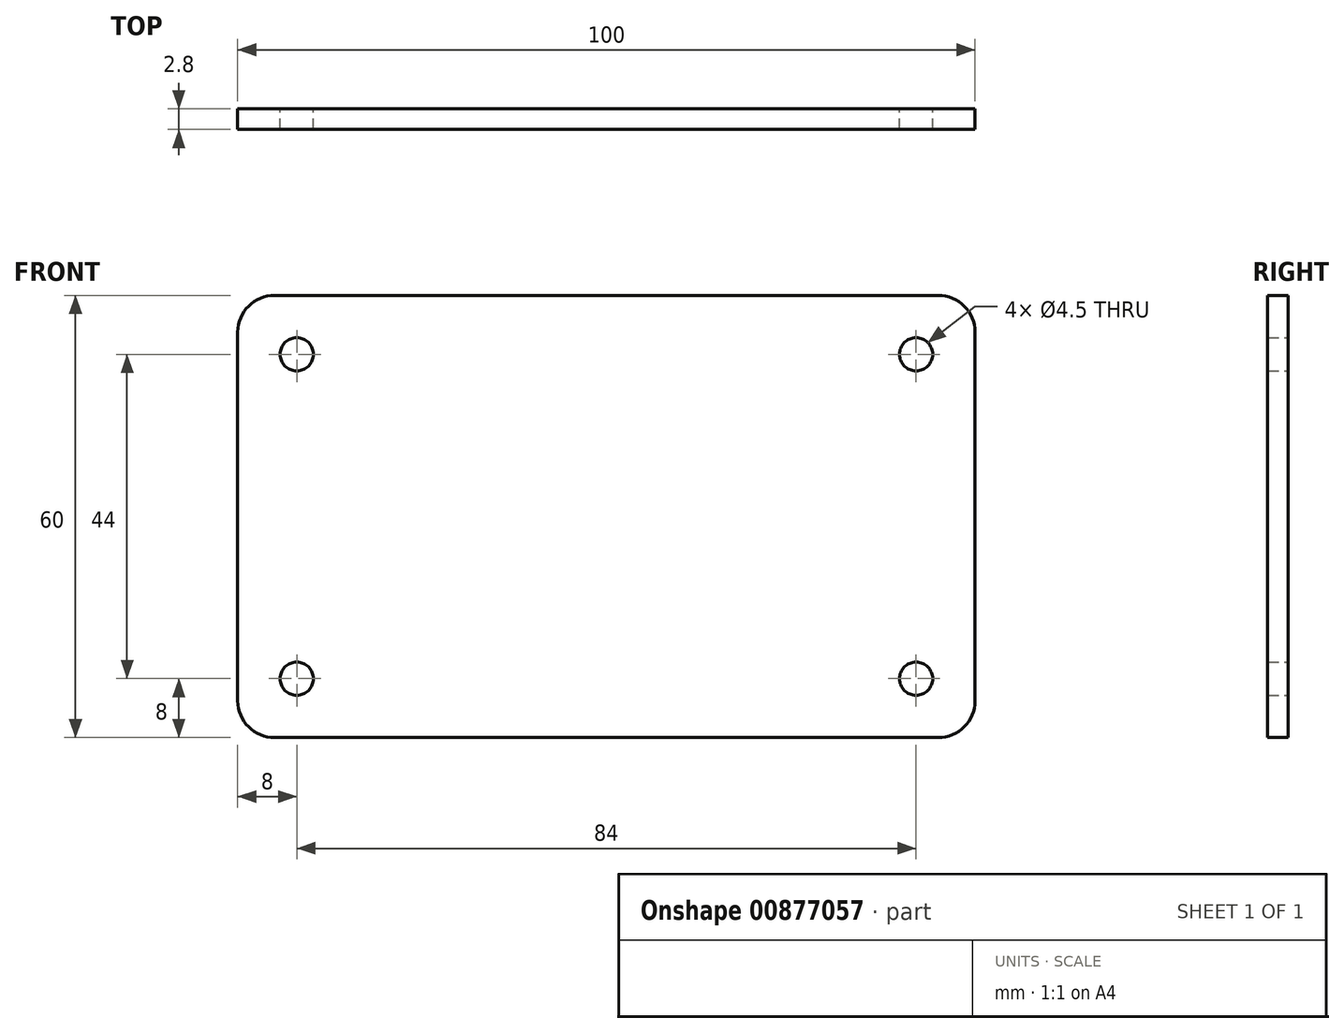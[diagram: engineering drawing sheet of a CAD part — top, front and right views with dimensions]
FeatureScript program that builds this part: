
annotation { "Feature Type Name" : "Feature", "Feature Type Description" : "" }
export const myFeature = defineFeature(function(context is Context, id is Id, definition is map)
    precondition{}
    {
        {
            var Q0;
            Q0=qCreatedBy(makeId("Front.planeOp"),FACE);
            var sketch = newSketch(context, id + "F0", { "sketchPlane" : qUnion([Q0])});
            skLineSegment(sketch, "E0.bottom", {"start": v(45, -30) * mm, "end": v(-45, -30) * mm});
            skLineSegment(sketch, "E0.top", {"start": v(45, 30) * mm, "end": v(-45, 30) * mm});
            skLineSegment(sketch, "E0.left", {"start": v(50, -25) * mm, "end": v(50, 25) * mm});
            skLineSegment(sketch, "E0.right", {"start": v(-50, -25) * mm, "end": v(-50, 25) * mm});
            skPoint(sketch, "E0.middle", {"position": v(0, 0) * mm});
            skLineSegment(sketch, "E1", {"start": v(0, 58.05) * mm, "end": v(0, -51.86) * mm, "construction": true});
            skCircle(sketch, "E2", {"center": v(-42, 22) * mm, "radius": 2.25 * mm});
            skCircle(sketch, "E3", {"center": v(-42, -22) * mm, "radius": 2.25 * mm});
            skCircle(sketch, "E4.MirrorC", {"center": v(42, 22) * mm, "radius": 2.25 * mm});
            skCircle(sketch, "E5.MirrorC", {"center": v(42, -22) * mm, "radius": 2.25 * mm});
            skPoint(sketch, "E6.visualSharp", {"position": v(-50, 30) * mm});
            skArc(sketch, "E6.filletArc", {"start": v(-45, 30) * mm, "mid": v(-48.54, 28.54) * mm, "end": v(-50, 25) * mm});
            skPoint(sketch, "E7.visualSharp", {"position": v(-50, -30) * mm});
            skArc(sketch, "E7.filletArc", {"start": v(-50, -25) * mm, "mid": v(-48.54, -28.54) * mm, "end": v(-45, -30) * mm});
            skPoint(sketch, "E8.visualSharp", {"position": v(50, -30) * mm});
            skArc(sketch, "E8.filletArc", {"start": v(45, -30) * mm, "mid": v(48.54, -28.54) * mm, "end": v(50, -25) * mm});
            skPoint(sketch, "E9.visualSharp", {"position": v(50, 30) * mm});
            skArc(sketch, "E9.filletArc", {"start": v(50, 25) * mm, "mid": v(48.54, 28.54) * mm, "end": v(45, 30) * mm});
            skArc(sketch, "E10.0", {"start": v(47, 25) * mm, "mid": v(46.41, 26.41) * mm, "end": v(45, 27) * mm});
            skLineSegment(sketch, "E10.1", {"start": v(47, -25) * mm, "end": v(47, 25) * mm});
            skLineSegment(sketch, "E10.2", {"start": v(45, 27) * mm, "end": v(-45, 27) * mm});
            skArc(sketch, "E10.3", {"start": v(45, -27) * mm, "mid": v(46.41, -26.41) * mm, "end": v(47, -25) * mm});
            skArc(sketch, "E10.4", {"start": v(-45, 27) * mm, "mid": v(-46.41, 26.41) * mm, "end": v(-47, 25) * mm});
            skLineSegment(sketch, "E10.5", {"start": v(-47, -25) * mm, "end": v(-47, 25) * mm});
            skArc(sketch, "E10.6", {"start": v(-47, -25) * mm, "mid": v(-46.41, -26.41) * mm, "end": v(-45, -27) * mm});
            skLineSegment(sketch, "E10.7", {"start": v(45, -27) * mm, "end": v(-45, -27) * mm});
            skSolve(sketch);
        }
        {
            var Q0;
            Q0=makeQuery(id+"F0.imprint","IMPRINT",FACE,{"disambiguationData":[TD([[makeQuery(id+"F0.imprint","IMPRINT",EDGE,{"derivedFrom":sQuery(id+"F0.wireOp",EDGE,"E0.bottom")}),-1.0]])]});
            var Q1;
            Q1=makeQuery(id+"F0.imprint","IMPRINT",FACE,{"disambiguationData":[TD([[makeQuery(id+"F0.imprint","IMPRINT",EDGE,{"derivedFrom":sQuery(id+"F0.wireOp",EDGE,"E2")}),-1.0]])]});
            extrude(context, id + "F1", {"entities" : qUnion([Q0, Q1]), "depth" : 2.8 * mm, "offsetDistance" : 25 * mm});
        }
    });
